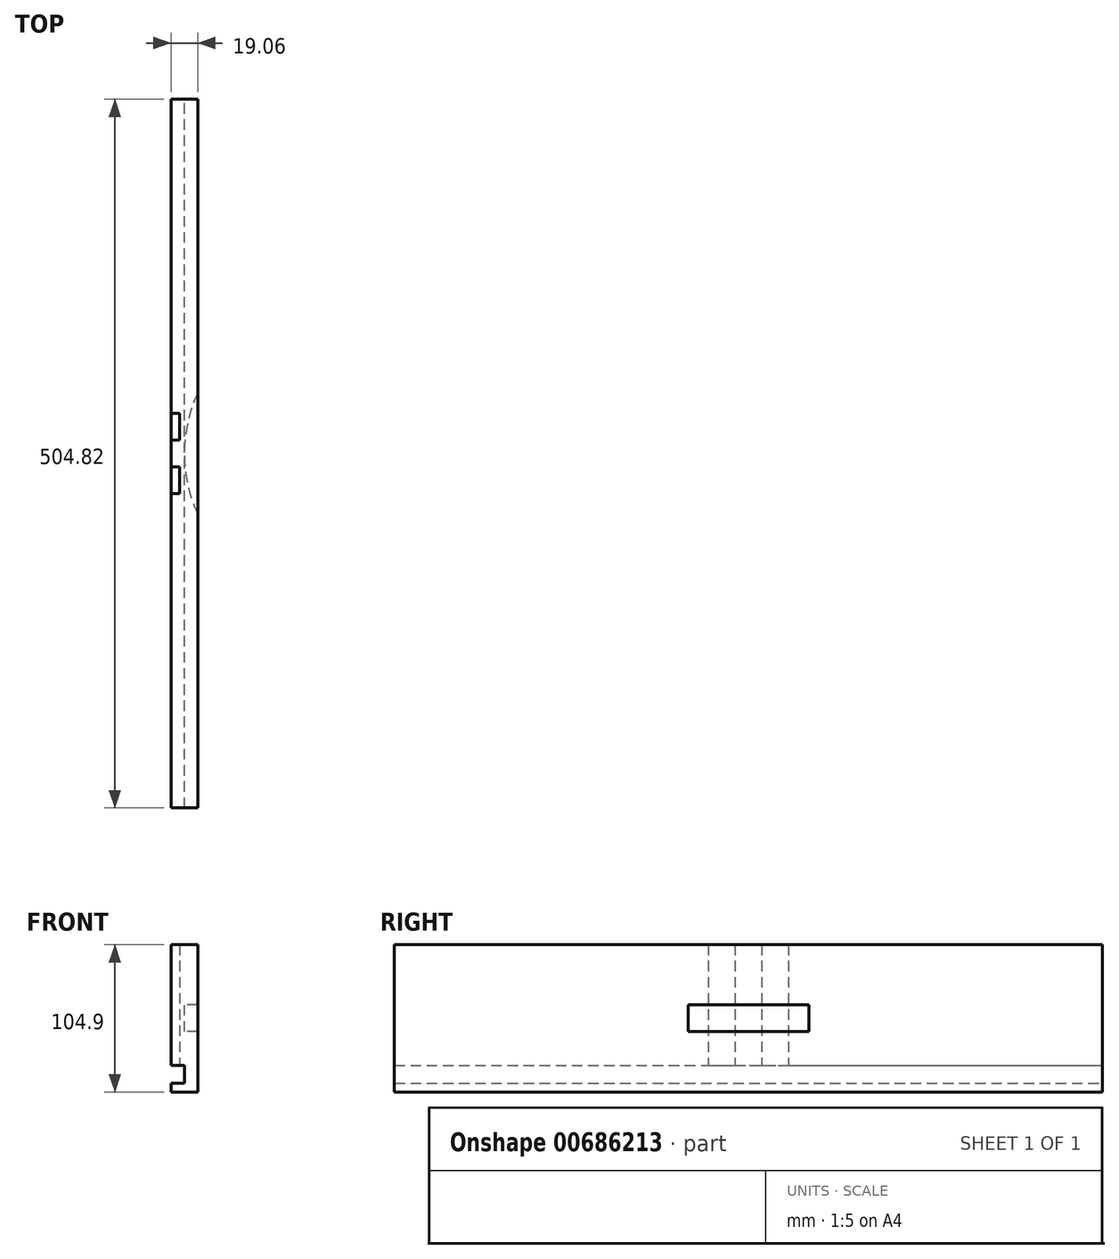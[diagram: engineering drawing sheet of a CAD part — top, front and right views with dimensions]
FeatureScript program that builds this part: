
annotation { "Feature Type Name" : "Feature", "Feature Type Description" : "" }
export const myFeature = defineFeature(function(context is Context, id is Id, definition is map)
    precondition{}
    {
        {
            var Q0;
            Q0=qCreatedBy(makeId("Front.planeOp"),FACE);
            var sketch = newSketch(context, id + "F0", { "sketchPlane" : qUnion([Q0])});
            skLineSegment(sketch, "E0.bottom", {"start": v(-9.53, 52.45) * mm, "end": v(9.52, 52.45) * mm});
            skLineSegment(sketch, "E0.top", {"start": v(-9.53, -52.45) * mm, "end": v(9.52, -52.45) * mm});
            skLineSegment(sketch, "E0.left", {"start": v(-9.53, 52.45) * mm, "end": v(-9.53, -33.4) * mm});
            skLineSegment(sketch, "E0.right", {"start": v(9.52, 52.45) * mm, "end": v(9.52, -52.45) * mm});
            skPoint(sketch, "E0.middle", {"position": v(0, 0) * mm});
            skLineSegment(sketch, "E1", {"start": v(-9.53, 52.45) * mm, "end": v(-32.23, 52.45) * mm, "construction": true});
            skLineSegment(sketch, "E2", {"start": v(-32.23, 52.45) * mm, "end": v(-32.23, 31.47) * mm, "construction": true});
            skLineSegment(sketch, "E3", {"start": v(-32.23, 31.47) * mm, "end": v(-9.53, 31.47) * mm, "construction": true});
            skLineSegment(sketch, "E4", {"start": v(-9.53, 31.47) * mm, "end": v(-9.53, 10.5) * mm, "construction": true});
            skLineSegment(sketch, "E5", {"start": v(-9.53, 10.5) * mm, "end": v(-32.23, 10.5) * mm, "construction": true});
            skLineSegment(sketch, "E6", {"start": v(-32.23, 10.5) * mm, "end": v(-32.23, -10.5) * mm, "construction": true});
            skLineSegment(sketch, "E7", {"start": v(-32.23, -10.5) * mm, "end": v(-9.53, -10.5) * mm, "construction": true});
            skLineSegment(sketch, "E8", {"start": v(-9.53, -10.5) * mm, "end": v(-9.53, -31.47) * mm, "construction": true});
            skLineSegment(sketch, "E9", {"start": v(-9.53, -31.47) * mm, "end": v(-32.23, -31.47) * mm, "construction": true});
            skLineSegment(sketch, "E10", {"start": v(-32.23, -31.47) * mm, "end": v(-32.23, -52.45) * mm, "construction": true});
            skLineSegment(sketch, "E11", {"start": v(-32.23, -52.45) * mm, "end": v(-9.53, -52.45) * mm, "construction": true});
            skLineSegment(sketch, "E12", {"start": v(-32.23, 31.47) * mm, "end": v(-32.23, 10.5) * mm, "construction": true});
            skLineSegment(sketch, "E13", {"start": v(-32.23, -10.5) * mm, "end": v(-32.23, -31.47) * mm, "construction": true});
            skLineSegment(sketch, "E14", {"start": v(-9.53, -33.4) * mm, "end": v(0, -33.4) * mm});
            skLineSegment(sketch, "E15", {"start": v(0, -33.4) * mm, "end": v(0, -46.1) * mm});
            skLineSegment(sketch, "E16", {"start": v(0, -46.1) * mm, "end": v(-9.53, -46.1) * mm});
            skLineSegment(sketch, "E17.trimOffspring", {"start": v(-9.53, -46.1) * mm, "end": v(-9.53, -52.45) * mm});
            skSolve(sketch);
        }
        {
            var Q0;
            Q0=makeQuery(id+"F0.imprint","IMPRINT",FACE,{"disambiguationData":[TD([[makeQuery(id+"F0.imprint","IMPRINT",EDGE,{"derivedFrom":sQuery(id+"F0.wireOp",EDGE,"E0.bottom")}),-1.0]])]});
            extrude(context, id + "F1", {"entities" : qUnion([Q0]), "depth" : 252.4 * mm, "offsetDistance" : 25.4 * mm});
        }
        {
            var Q0;
            Q0=makeQuery(id+"F1.opExtrude","SWEPT_FACE",FACE,{"disambiguationData":[OSD([sQuery(id+"F0.wireOp",EDGE,"E0.right")])]});
            var sketch = newSketch(context, id + "F2", { "sketchPlane" : qUnion([Q0])});
            skLineSegment(sketch, "E18.bottom", {"start": v(-252.41, 52.45) * mm, "end": v(-233.36, 52.45) * mm});
            skLineSegment(sketch, "E18.top", {"start": v(-252.41, 31.47) * mm, "end": v(-233.36, 31.47) * mm});
            skLineSegment(sketch, "E18.left", {"start": v(-252.41, 52.45) * mm, "end": v(-252.41, 31.47) * mm});
            skLineSegment(sketch, "E18.right", {"start": v(-233.36, 52.45) * mm, "end": v(-233.36, 31.47) * mm});
            skLineSegment(sketch, "E19.bottom", {"start": v(-252.41, 10.5) * mm, "end": v(-233.36, 10.5) * mm});
            skLineSegment(sketch, "E19.top", {"start": v(-252.41, -10.5) * mm, "end": v(-233.36, -10.5) * mm});
            skLineSegment(sketch, "E19.left", {"start": v(-252.41, 10.5) * mm, "end": v(-252.41, -10.5) * mm});
            skLineSegment(sketch, "E19.right", {"start": v(-233.36, 10.5) * mm, "end": v(-233.36, -10.5) * mm});
            skLineSegment(sketch, "E20.bottom", {"start": v(-252.41, -31.47) * mm, "end": v(-233.36, -31.47) * mm});
            skLineSegment(sketch, "E20.top", {"start": v(-252.41, -52.45) * mm, "end": v(-233.36, -52.45) * mm});
            skLineSegment(sketch, "E20.left", {"start": v(-252.41, -31.47) * mm, "end": v(-252.41, -52.45) * mm});
            skLineSegment(sketch, "E20.right", {"start": v(-233.36, -31.47) * mm, "end": v(-233.36, -52.45) * mm});
            skLineSegment(sketch, "E21", {"start": v(-233.36, 31.47) * mm, "end": v(-233.36, 10.5) * mm, "construction": true});
            skLineSegment(sketch, "E22", {"start": v(-233.36, -10.5) * mm, "end": v(-233.36, -31.47) * mm, "construction": true});
            skSolve(sketch);
        }
        {
            var Q0;
            Q0=makeQuery(id+"F1.opExtrude","SWEPT_BODY",BODY,{"disambiguationData":[OSD([sQuery(id+"F0.wireOp",EDGE,"E0.bottom"),sQuery(id+"F0.wireOp",EDGE,"E0.top"),sQuery(id+"F0.wireOp",EDGE,"E0.left"),sQuery(id+"F0.wireOp",EDGE,"E0.right")])]});
            var Q1;
            Q1=qCreatedBy(makeId("Front.planeOp"),FACE);
            mirror(context, id + "F3", {"operationType" : NewBodyOperationType.ADD, "entities" : qUnion([Q0]), "mirrorPlane" : qUnion([Q1])});
        }
        {
            var Q0;
            Q0=qCreatedBy(makeId("Top.planeOp"),FACE);
            var sketch = newSketch(context, id + "F4", { "sketchPlane" : qUnion([Q0])});
            skCircle(sketch, "E23", {"center": v(101.6, 0) * mm, "radius": 101.6 * mm});
            skSolve(sketch);
        }
        {
            var Q0;
            Q0 = qSketchRegion(id + "F4", true);
            extrude(context, id + "F5", {"entities" : qUnion([Q0]), "operationType" : NewBodyOperationType.REMOVE, "endBound" : BoundingType.SYMMETRIC, "oppositeDirection" : true, "depth" : 19.05 * mm, "offsetDistance" : 25.4 * mm});
        }
        {
            var Q0;
            {var subQ0=makeQuery(id+"F1.opExtrude","SWEPT_FACE",FACE,{"disambiguationData":[OSD([sQuery(id+"F0.wireOp",EDGE,"E0.left")])]});Q0=makeQuery(id+"F3.boolean.opBoolean","MERGE",FACE,{"derivedFrom":[subQ0,makeQuery(id+"F3.opPattern","COPY",FACE,{"derivedFrom":subQ0,"instanceName":"1"})]});}
            var sketch = newSketch(context, id + "F6", { "sketchPlane" : qUnion([Q0])});
            skLineSegment(sketch, "E24.bottom", {"start": v(-28.57, 52.45) * mm, "end": v(-9.52, 52.45) * mm});
            skLineSegment(sketch, "E24.top", {"start": v(-28.57, -33.4) * mm, "end": v(-9.52, -33.4) * mm});
            skLineSegment(sketch, "E24.left", {"start": v(-28.57, 52.45) * mm, "end": v(-28.57, -33.4) * mm});
            skLineSegment(sketch, "E24.right", {"start": v(-9.52, 52.45) * mm, "end": v(-9.52, -33.4) * mm});
            skLineSegment(sketch, "E25", {"start": v(0, 78.61) * mm, "end": v(0, -93.88) * mm, "construction": true});
            skLineSegment(sketch, "E26.MirrorCS", {"start": v(28.57, 52.45) * mm, "end": v(9.52, 52.45) * mm});
            skLineSegment(sketch, "E27.MirrorCS", {"start": v(28.57, 52.45) * mm, "end": v(28.57, -33.4) * mm});
            skLineSegment(sketch, "E28.MirrorCS", {"start": v(9.52, 52.45) * mm, "end": v(9.52, -33.4) * mm});
            skLineSegment(sketch, "E29.MirrorCS", {"start": v(28.57, -33.4) * mm, "end": v(9.52, -33.4) * mm});
            skSolve(sketch);
        }
        {
            var Q0;
            Q0 = qSketchRegion(id + "F6", true);
            extrude(context, id + "F7", {"entities" : qUnion([Q0]), "operationType" : NewBodyOperationType.REMOVE, "oppositeDirection" : true, "depth" : 6.35 * mm, "offsetDistance" : 25.4 * mm});
        }
    });
